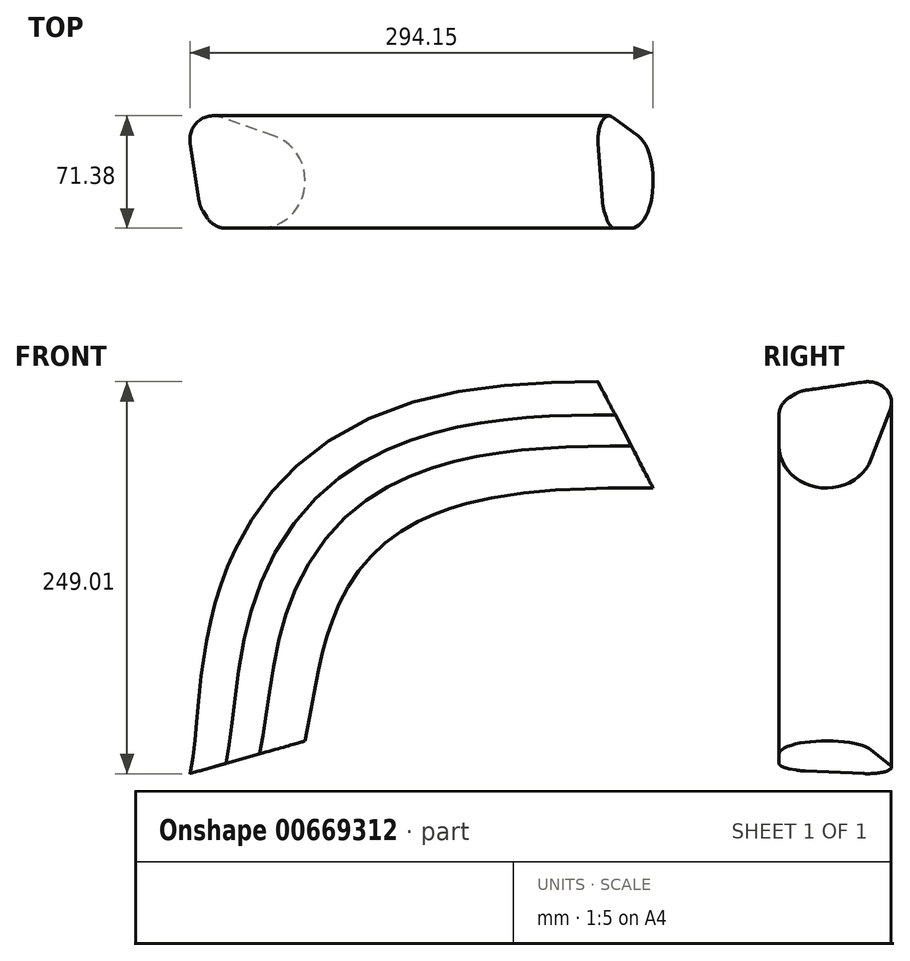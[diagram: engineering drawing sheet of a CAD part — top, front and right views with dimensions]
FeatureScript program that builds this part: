
annotation { "Feature Type Name" : "Feature", "Feature Type Description" : "" }
export const myFeature = defineFeature(function(context is Context, id is Id, definition is map)
    precondition{}
    {
        {
            var Q0;
            Q0=qCreatedBy(makeId("Top.planeOp"),FACE);
            var sketch = newSketch(context, id + "F0", { "sketchPlane" : qUnion([Q0])});
            skLineSegment(sketch, "E0", {"start": v(-122.3, -10.78) * mm, "end": v(-119.47, -14.95) * mm});
            skLineSegment(sketch, "E1", {"start": v(-107.05, -21.55) * mm, "end": v(-84.73, -21.55) * mm});
            skLineSegment(sketch, "E2", {"start": v(-75.1, 36.86) * mm, "end": v(-110.99, 49.03) * mm});
            skLineSegment(sketch, "E3", {"start": v(-130.62, 32.46) * mm, "end": v(-124.68, -4.75) * mm});
            skPoint(sketch, "E4.visualSharp", {"position": v(97.16, -21.55) * mm});
            skArc(sketch, "E4.filletArc", {"start": v(-84.73, -21.55) * mm, "mid": v(-55.13, 3.57) * mm, "end": v(-75.1, 36.86) * mm});
            skPoint(sketch, "E5.visualSharp", {"position": v(-134.54, 57.02) * mm});
            skArc(sketch, "E5.filletArc", {"start": v(-110.99, 49.03) * mm, "mid": v(-125.48, 46.29) * mm, "end": v(-130.62, 32.46) * mm});
            skPoint(sketch, "E6.visualSharp", {"position": v(-124.15, -8.03) * mm});
            skArc(sketch, "E6.filletArc", {"start": v(-124.68, -4.75) * mm, "mid": v(-123.81, -7.9) * mm, "end": v(-122.3, -10.78) * mm});
            skPoint(sketch, "E7.visualSharp", {"position": v(-115.01, -21.55) * mm});
            skArc(sketch, "E7.filletArc", {"start": v(-119.47, -14.95) * mm, "mid": v(-114.08, -19.8) * mm, "end": v(-107.05, -21.55) * mm});
            skSolve(sketch);
        }
        {
            var Q0;
            Q0=qCreatedBy(makeId("Front.planeOp"),FACE);
            var sketch = newSketch(context, id + "F1", { "sketchPlane" : qUnion([Q0])});
            skFitSpline(sketch, "E8", {"points": [v(-18.13, -53.4) * mm, v(17.52, 23.27) * mm, v(176.32, 45.85) * mm], "startDerivative": vector(44.93, 212.4) * mm, "endDerivative": vector(328.94, -2.55) * mm});
            skSolve(sketch);
        }
        {
            var Q0;
            Q0 = qSketchRegion(id + "F0", true);
            var Q1;
            Q1 = qConstructionFilter(qBodyType(qCreatedBy(id + "F1" ,EDGE), BodyType.WIRE), ConstructionObject.NO);
            sweep(context, id + "F2", {"profiles" : qUnion([Q0]), "path" : qUnion([Q1])});
        }
    });
